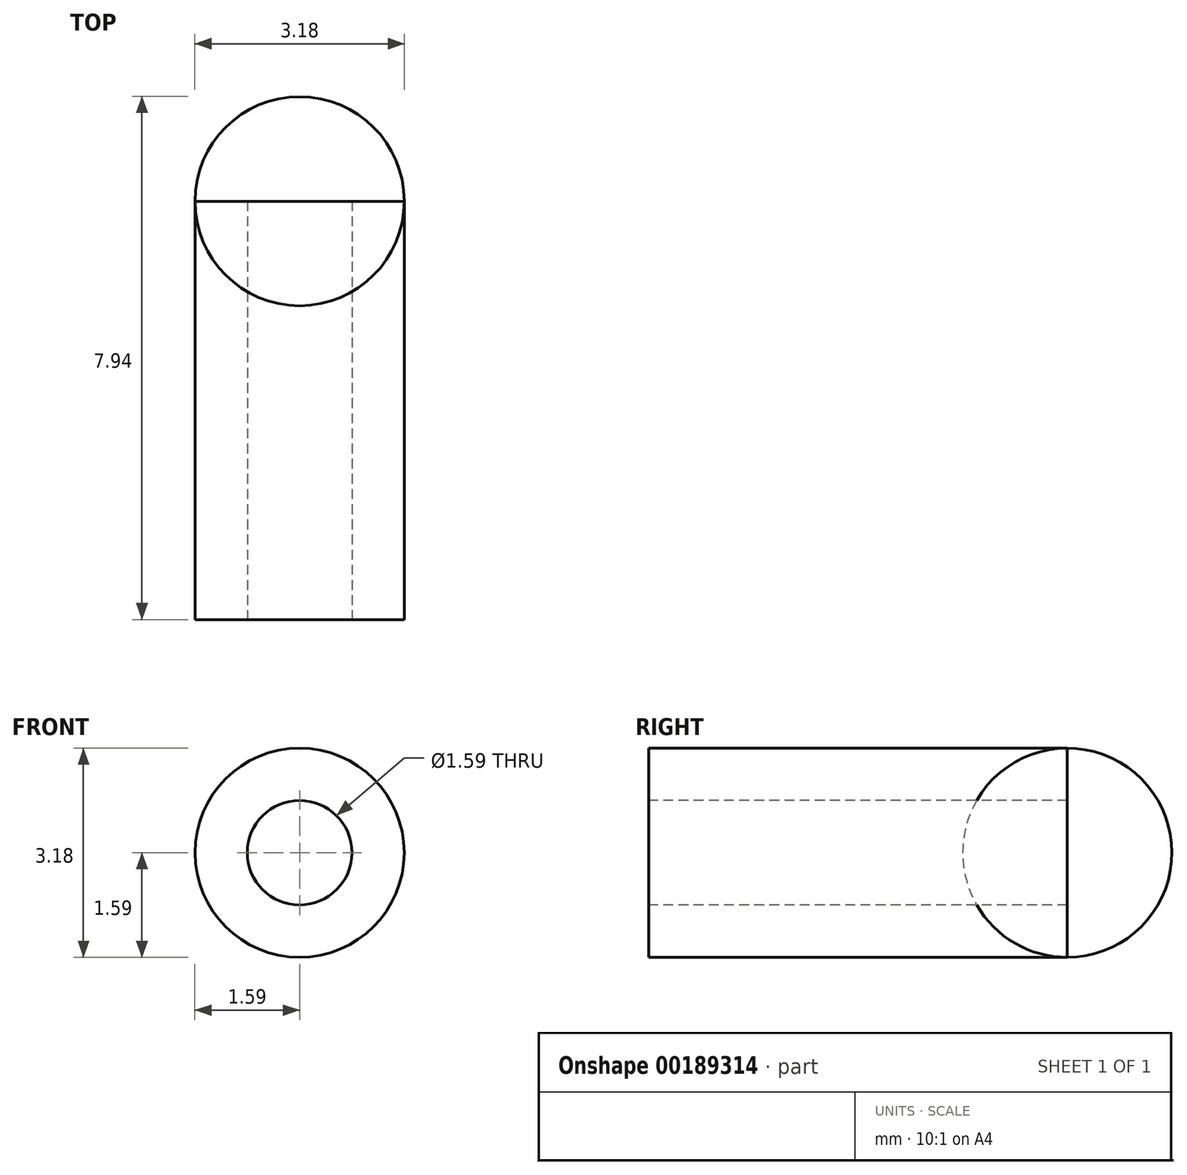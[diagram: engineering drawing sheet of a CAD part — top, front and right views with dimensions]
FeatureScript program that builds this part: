
annotation { "Feature Type Name" : "Feature", "Feature Type Description" : "" }
export const myFeature = defineFeature(function(context is Context, id is Id, definition is map)
    precondition{}
    {
        {
            var Q0;
            Q0=qCreatedBy(makeId("Front.planeOp"),FACE);
            var sketch = newSketch(context, id + "F0", { "sketchPlane" : qUnion([Q0])});
            skCircle(sketch, "E0", {"center": v(0, 0) * mm, "radius": 1.59 * mm});
            skCircle(sketch, "E1", {"center": v(0, 0) * mm, "radius": 0.8 * mm});
            skSolve(sketch);
        }
        {
            var Q0;
            Q0=makeQuery(id+"F0.imprint","IMPRINT",FACE,{"disambiguationData":[TD([[makeQuery(id+"F0.imprint","IMPRINT",EDGE,{"derivedFrom":sQuery(id+"F0.wireOp",EDGE,"E0")}),1.0]])]});
            extrude(context, id + "F1", {"entities" : qUnion([Q0]), "oppositeDirection" : true, "depth" : 6.35 * mm});
        }
        {
            var Q0;
            Q0=makeQuery(id+"F0.imprint","IMPRINT",FACE,{"disambiguationData":[TD([[makeQuery(id+"F0.imprint","IMPRINT",EDGE,{"derivedFrom":sQuery(id+"F0.wireOp",EDGE,"E1")}),1.0]])]});
            var Q1;
            Q1=makeQuery(id+"F0.imprint","IMPRINT",FACE,{"disambiguationData":[TD([[makeQuery(id+"F0.imprint","IMPRINT",EDGE,{"derivedFrom":sQuery(id+"F0.wireOp",EDGE,"E0")}),1.0]])]});
            extrude(context, id + "F2", {"entities" : qUnion([Q0, Q1]), "oppositeDirection" : true, "depth" : 6.35 * mm});
        }
        {
            var Q0;
            Q0=makeQuery(id+"F2.opExtrude","CAP_FACE",FACE,{"disambiguationData":[OSD([sQuery(id+"F0.wireOp",EDGE,"E0")])],"isStart":false});
            var sketch = newSketch(context, id + "F3", { "sketchPlane" : qUnion([Q0])});
            skArc(sketch, "E2", {"start": v(1.59, 0) * mm, "mid": v(0, 1.59) * mm, "end": v(-1.59, 0) * mm});
            skLineSegment(sketch, "E3", {"start": v(-1.59, 0) * mm, "end": v(1.59, 0) * mm});
            skSolve(sketch);
        }
        {
            var Q0;
            Q0=makeQuery(id+"F3.imprint","IMPRINT",FACE,{"disambiguationData":[TD([[makeQuery(id+"F3.imprint","IMPRINT",EDGE,{"derivedFrom":sQuery(id+"F3.wireOp",EDGE,"E2")}),-1.0]])]});
            var Q1;
            Q1=sQuery(id+"F3.wireOp",EDGE,"E3");
            revolve(context, id + "F4", {"entities" : qUnion([Q0]), "axis" : qUnion([Q1]), "revolveType" : RevolveType.FULL});
        }
    });
